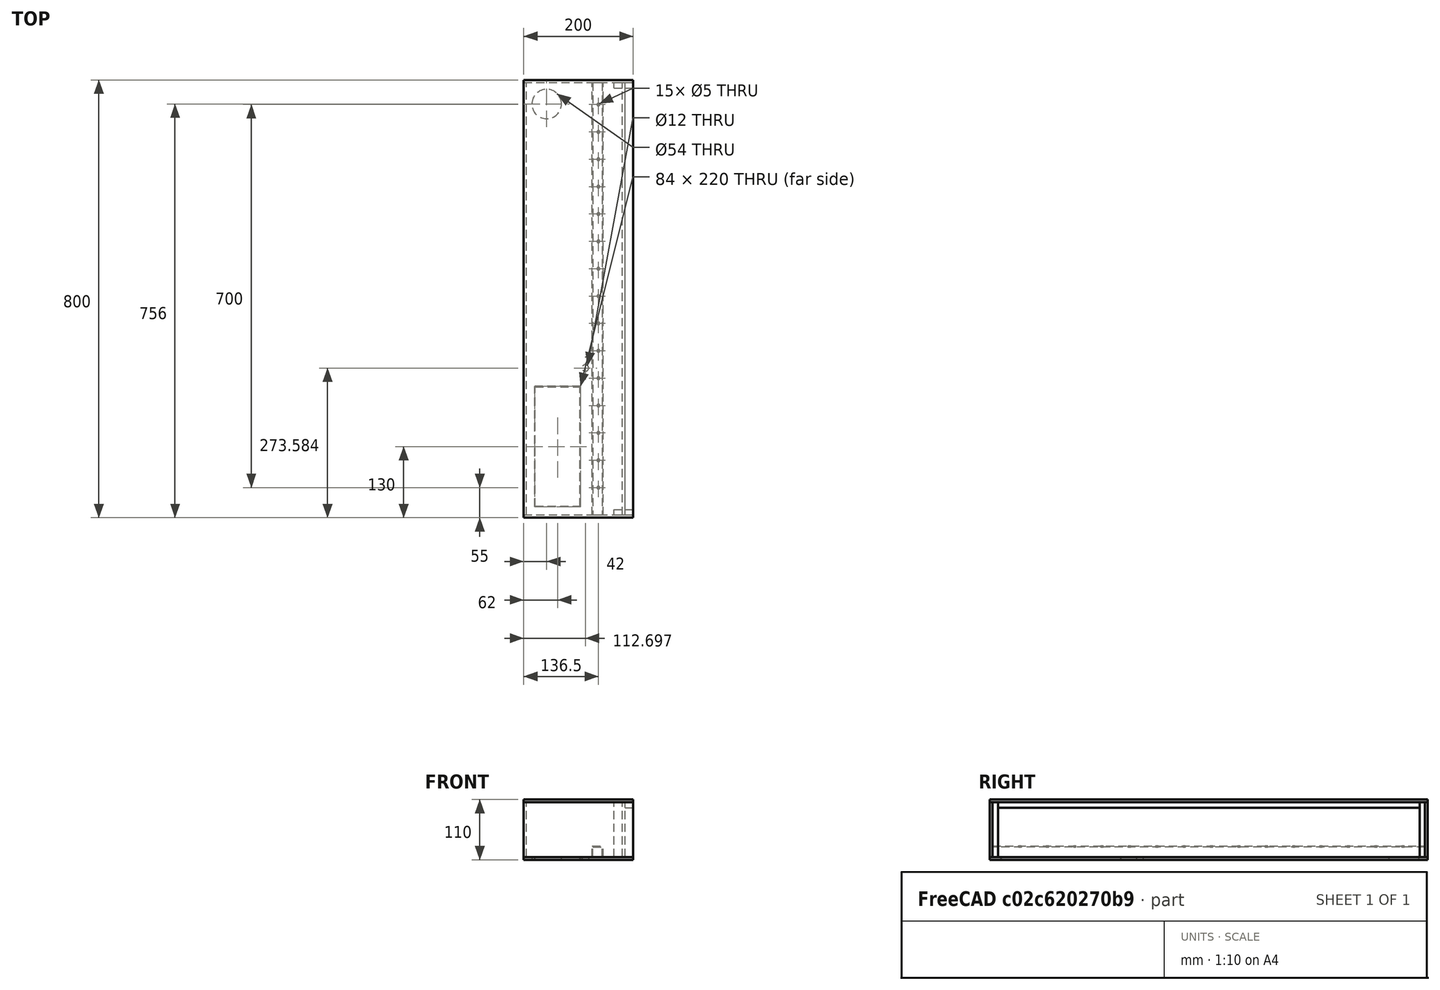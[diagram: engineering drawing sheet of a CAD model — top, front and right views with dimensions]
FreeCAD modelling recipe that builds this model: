
FCSTD DOCUMENT  (FreeCAD 0.20R29177 (Git))
Label: camera_trap_v5
License: All rights reserved
LicenseURL: http://en.wikipedia.org/wiki/All_rights_reserved
objects: Part::Box×13, PartDesign::FeatureBase×2, PartDesign::SubtractiveBox×2, Sketcher::SketchObject×2, PartDesign::Hole×2, PartDesign::Body×2, App::Part×1, PartDesign::SubtractiveCylinder×1
note: 29 computed .brp shape members not serialized (recipe doc carries the construction recipe); baked Part::Feature solids carry a one-line shape summary decoded from their .brp

FEATURE [App::Part] Part
  Origin = -> Origin
FEATURE [Part::Box] Box  label="Roof"
  AttacherType = Attacher::AttachEngine3D
  Height = 5
  Length = 200
  Placement = pos=(0,0,105) rot=(0,0,1;0rad)
  Width = 800
FEATURE [Part::Box] Box001  label="Floor_base"
  AttacherType = Attacher::AttachEngine3D
  Height = 5
  Length = 200
  Width = 800
FEATURE [Part::Box] Box002  label="Glass"
  AttacherType = Attacher::AttachEngine3D
  Height = 100
  Length = 5
  Placement = pos=(180,5,5) rot=(0,0,1;0rad)
  Width = 790
FEATURE [Part::Box] Box003  label="SideRight"
  AttacherType = Attacher::AttachEngine3D
  Height = 100
  Length = 200
  Placement = pos=(0,0,5) rot=(0,0,1;0rad)
  Width = 5
FEATURE [Part::Box] Box004  label="SideLeft"
  AttacherType = Attacher::AttachEngine3D
  Height = 100
  Length = 200
  Placement = pos=(0,795,5) rot=(0,0,1;0rad)
  Width = 5
FEATURE [Part::Box] Box005  label="Back"
  AttacherType = Attacher::AttachEngine3D
  Height = 100
  Length = 5
  Placement = pos=(0,5,5) rot=(0,0,1;0rad)
  Width = 790
FEATURE [Part::Box] Box007  label="vbar1"
  AttacherType = Attacher::AttachEngine3D
  Height = 100
  Length = 15
  Placement = pos=(185,5,5) rot=(0,0,1;0rad)
  Width = 10
FEATURE [Part::Box] Box008  label="vbar2"
  AttacherType = Attacher::AttachEngine3D
  Height = 100
  Length = 15
  Placement = pos=(165,5,5) rot=(0,0,1;0rad)
  Width = 10
FEATURE [Part::Box] Box009  label="vbar3"
  AttacherType = Attacher::AttachEngine3D
  Height = 100
  Length = 15
  Placement = pos=(185,785,5) rot=(0,0,1;0rad)
  Width = 10
FEATURE [Part::Box] Box010  label="vbar4"
  AttacherType = Attacher::AttachEngine3D
  Height = 100
  Length = 15
  Placement = pos=(165,785,5) rot=(0,0,1;0rad)
  Width = 10
FEATURE [Part::Box] Box006  label="Rail_base"
  AttacherType = Attacher::AttachEngine3D
  Height = 20
  Length = 20
  Placement = pos=(145,5,85) rot=(0,0,1;0rad)
  Width = 790
FEATURE [PartDesign::FeatureBase] BaseFeature
  BaseFeature = -> Box006
FEATURE [PartDesign::SubtractiveBox] Box011
  AttacherType = Attacher::AttachEngine3D
  AttachmentOffset = pos=(1.5,0,-800) rot=(0,0,1;0rad)
  BaseFeature = -> BaseFeature
  Height = 800
  Length = 17
  MapMode = 5
  Placement = pos=(1.5,800,-1.776e-13) rot=(1,0,0;1.5708rad)
  Support = -> [BaseFeature]
  Width = 18.5
FEATURE [Sketcher::SketchObject] Sketch
  FullyConstrained = false
  MapMode = 3
  Placement = pos=(1.5,800,-1.78e-13) rot=(1,0,0;3.14159rad)
  sketch-geometry (15):
    g0: Circle CenterX=10 CenterY=50 CenterZ=0 NormalX=0 NormalY=0 NormalZ=1 AngleXU=0 Radius=3
    g1: Circle CenterX=10 CenterY=100 CenterZ=0 NormalX=0 NormalY=0 NormalZ=1 AngleXU=0 Radius=3
    g2: Circle CenterX=10 CenterY=150 CenterZ=0 NormalX=0 NormalY=0 NormalZ=1 AngleXU=0 Radius=2.99551
    g3: Circle CenterX=10 CenterY=200 CenterZ=0 NormalX=0 NormalY=0 NormalZ=1 AngleXU=0 Radius=2.99072
    g4: Circle CenterX=10 CenterY=250 CenterZ=0 NormalX=0 NormalY=0 NormalZ=1 AngleXU=0 Radius=2.99074
    g5: Circle CenterX=10 CenterY=300 CenterZ=0 NormalX=0 NormalY=0 NormalZ=1 AngleXU=0 Radius=2.95606
    g6: Circle CenterX=10 CenterY=350 CenterZ=0 NormalX=0 NormalY=0 NormalZ=1 AngleXU=0 Radius=2.95608
    g7: Circle CenterX=10 CenterY=400 CenterZ=0 NormalX=0 NormalY=0 NormalZ=1 AngleXU=0 Radius=3.02504
    g8: Circle CenterX=10 CenterY=450 CenterZ=0 NormalX=0 NormalY=0 NormalZ=1 AngleXU=0 Radius=3.01134
    g9: Circle CenterX=10 CenterY=500 CenterZ=0 NormalX=0 NormalY=0 NormalZ=1 AngleXU=0 Radius=2.9708
    g10: Circle CenterX=10 CenterY=550 CenterZ=0 NormalX=0 NormalY=0 NormalZ=1 AngleXU=0 Radius=2.97082
    g11: Circle CenterX=10 CenterY=600 CenterZ=0 NormalX=0 NormalY=0 NormalZ=1 AngleXU=0 Radius=2.98133
    g12: Circle CenterX=10 CenterY=650 CenterZ=0 NormalX=0 NormalY=0 NormalZ=1 AngleXU=0 Radius=3.00958
    g13: Circle CenterX=10 CenterY=700 CenterZ=0 NormalX=0 NormalY=0 NormalZ=1 AngleXU=0 Radius=3.0096
    g14: Circle CenterX=10 CenterY=750 CenterZ=0 NormalX=0 NormalY=0 NormalZ=1 AngleXU=0 Radius=2.98631
FEATURE [PartDesign::Hole] Hole
  BaseFeature = -> Box011
  CustomThreadClearance = 0
  Depth = 25
  DepthType = 0
  Diameter = 5
  DrillForDepth = false
  DrillPoint = 0
  DrillPointAngle = 118
  HoleCutCountersinkAngle = 90
  HoleCutCustomValues = false
  HoleCutDepth = 0
  HoleCutDiameter = 6.1
  HoleCutType = 0
  ModelThread = false
  Placement = pos=(1.5,800,-1.78e-13) rot=(1,0,0;1.5708rad)
  Profile = -> Sketch
  Tapered = false
  TaperedAngle = 90
  ThreadClass = 0
  ThreadDepth = 25
  ThreadDepthType = 0
  ThreadDirection = 0
  ThreadFit = 0
  ThreadSize = 0
  ThreadType = 0
  Threaded = false
  UseCustomThreadClearance = false
FEATURE [PartDesign::Body] Body  label="Rail"
  BaseFeature = -> Box006
  Group = -> [BaseFeature,Box011,Sketch,Hole]
  Origin = -> Origin001
  Placement = pos=(125,5,5) rot=(0,0,1;0rad)
  Tip = -> Hole
FEATURE [PartDesign::FeatureBase] BaseFeature001
  BaseFeature = -> Box001
FEATURE [Sketcher::SketchObject] Sketch001
  FullyConstrained = false
  MapMode = 5
  Placement = pos=(0,0,5) rot=(0,0,1;0rad)
  Support = -> [BaseFeature001]
  sketch-geometry (1):
    g0: Circle CenterX=112.697 CenterY=273.584 CenterZ=0 NormalX=0 NormalY=0 NormalZ=1 AngleXU=0 Radius=6.80402
FEATURE [PartDesign::Hole] Hole001
  BaseFeature = -> BaseFeature001
  CustomThreadClearance = 0
  Depth = 31
  DepthType = 0
  Diameter = 12
  DrillForDepth = false
  DrillPoint = 1
  DrillPointAngle = 118
  HoleCutCountersinkAngle = 90
  HoleCutCustomValues = false
  HoleCutDepth = 0
  HoleCutDiameter = 6.1
  HoleCutType = 0
  ModelThread = false
  Profile = -> Sketch001
  Tapered = false
  TaperedAngle = 90
  ThreadClass = 0
  ThreadDepth = 31
  ThreadDepthType = 0
  ThreadDirection = 0
  ThreadFit = 0
  ThreadSize = 0
  ThreadType = 0
  Threaded = false
  UseCustomThreadClearance = false
FEATURE [PartDesign::SubtractiveCylinder] Cylinder
  Angle = 360
  AttacherType = Attacher::AttachEngine3D
  AttachmentOffset = pos=(42,756,-25) rot=(0,0,1;0rad)
  BaseFeature = -> Hole001
  FirstAngle = 0
  Height = 55
  MapMode = 5
  Placement = pos=(42,756,-20) rot=(0,0,1;0rad)
  Radius = 27
  SecondAngle = 0
  Support = -> [Hole001]
FEATURE [PartDesign::SubtractiveBox] Box012
  AttacherType = Attacher::AttachEngine3D
  AttachmentOffset = pos=(20,20,-10) rot=(0,0,1;0rad)
  BaseFeature = -> Cylinder
  Height = 20
  Length = 84
  MapMode = 5
  Placement = pos=(20,20,-10) rot=(0,0,1;0rad)
  Support = -> [XY_Plane002]
  Width = 220
FEATURE [PartDesign::Body] Body001  label="Floor"
  BaseFeature = -> Box001
  Group = -> [BaseFeature001,Sketch001,Hole001,Cylinder,Box012]
  Origin = -> Origin002
  Tip = -> Box012
FEATURE [Part::Box] Box013  label="door"
  AttacherType = Attacher::AttachEngine3D
  Height = 5
  Length = 82
  Placement = pos=(21,21,0) rot=(0,0,1;0rad)
  Width = 218
FEATURE [Part::Box] Box014  label="hbar"
  AttacherType = Attacher::AttachEngine3D
  Height = 10
  Length = 15
  Placement = pos=(185,15,95) rot=(0,0,1;0rad)
  Width = 770
